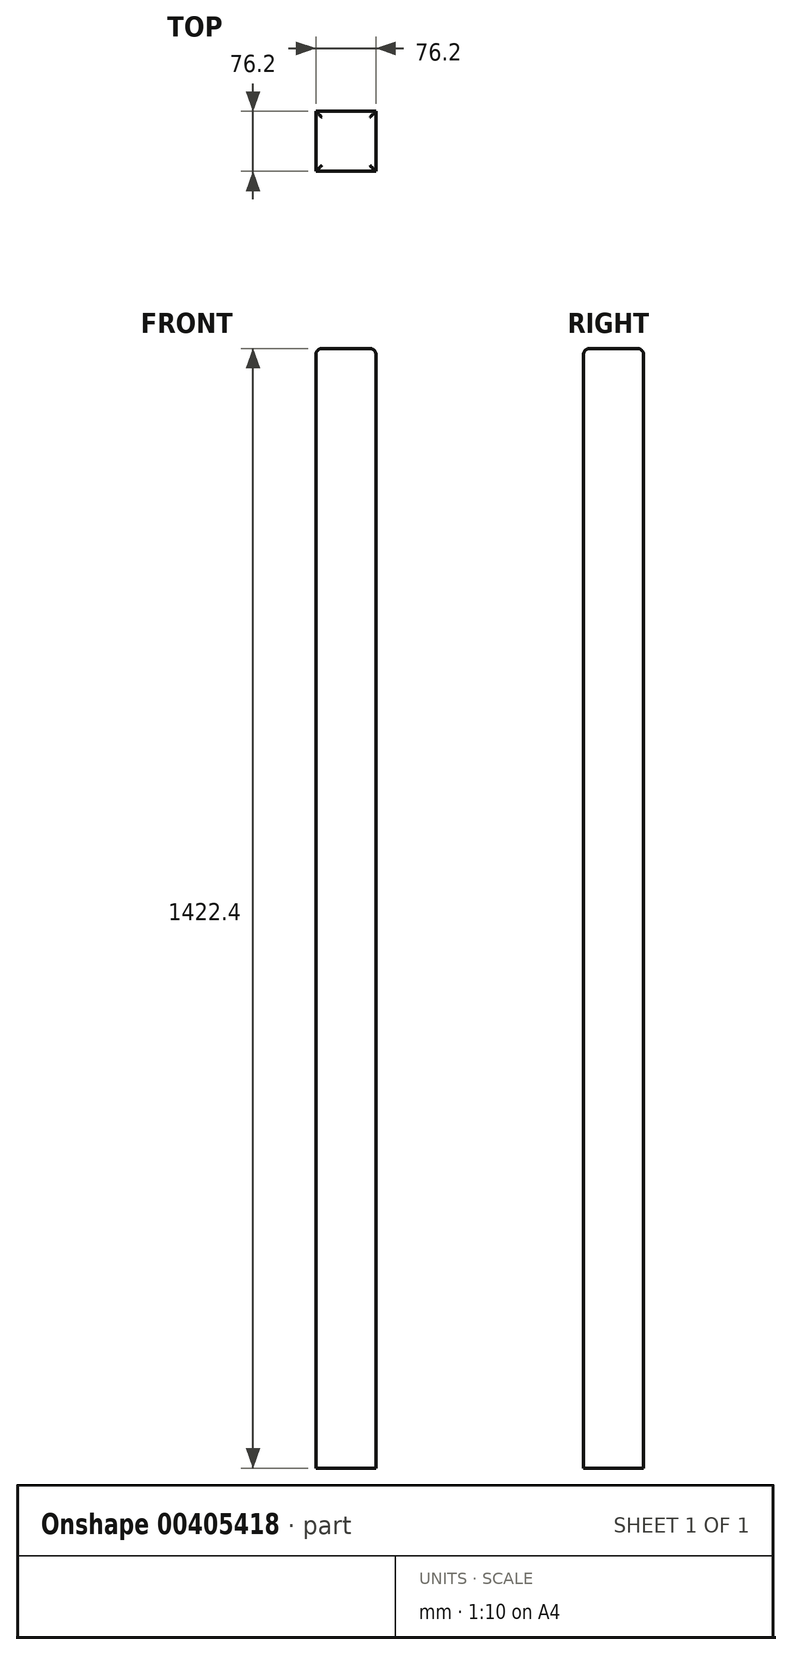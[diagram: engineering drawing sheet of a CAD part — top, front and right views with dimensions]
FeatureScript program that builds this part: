
annotation { "Feature Type Name" : "Feature", "Feature Type Description" : "" }
export const myFeature = defineFeature(function(context is Context, id is Id, definition is map)
    precondition{}
    {
        {
            var Q0;
            Q0=qCreatedBy(makeId("Front.planeOp"),FACE);
            var sketch = newSketch(context, id + "F0", { "sketchPlane" : qUnion([Q0])});
            skLineSegment(sketch, "E0.bottom", {"start": v(-38.1, 711.2) * mm, "end": v(38.1, 711.2) * mm});
            skLineSegment(sketch, "E0.top", {"start": v(-38.1, -711.2) * mm, "end": v(38.1, -711.2) * mm});
            skLineSegment(sketch, "E0.left", {"start": v(-38.1, 711.2) * mm, "end": v(-38.1, -711.2) * mm});
            skLineSegment(sketch, "E0.right", {"start": v(38.1, 711.2) * mm, "end": v(38.1, -711.2) * mm});
            skSolve(sketch);
        }
        {
            var Q0;
            Q0=makeQuery(id+"F0.imprint","IMPRINT",FACE,{"disambiguationData":[TD([[makeQuery(id+"F0.imprint","IMPRINT",EDGE,{"derivedFrom":sQuery(id+"F0.wireOp",EDGE,"E0.bottom")}),-1.0]])]});
            extrude(context, id + "F1", {"entities" : qUnion([Q0]), "depth" : 76.2 * mm, "symmetric" : true});
        }
        {
            var Q0;
            Q0=makeQuery(id+"F1.opExtrude","SWEPT_EDGE",EDGE,{"disambiguationData":[OSD([sQuery(id+"F0.wireOp",EDGE,"E0.bottom"),sQuery(id+"F0.wireOp",EDGE,"E0.right")])]});
            var Q1;
            Q1=makeQuery(id+"F1.opExtrude","CAP_EDGE",EDGE,{"disambiguationData":[OSD([sQuery(id+"F0.wireOp",EDGE,"E0.bottom")])],"isStart":false});
            var Q2;
            Q2=makeQuery(id+"F1.opExtrude","CAP_EDGE",EDGE,{"disambiguationData":[OSD([sQuery(id+"F0.wireOp",EDGE,"E0.bottom")])],"isStart":true});
            var Q3;
            Q3=makeQuery(id+"F1.opExtrude","SWEPT_EDGE",EDGE,{"disambiguationData":[OSD([sQuery(id+"F0.wireOp",EDGE,"E0.bottom"),sQuery(id+"F0.wireOp",EDGE,"E0.left")])]});
            fillet(context, id + "F2", {"entities" : qUnion([Q0, Q1, Q2, Q3]), "radius" : 7.62 * mm, "tangentPropagation" : true, "allowEdgeOverflow" : false});
        }
    });
